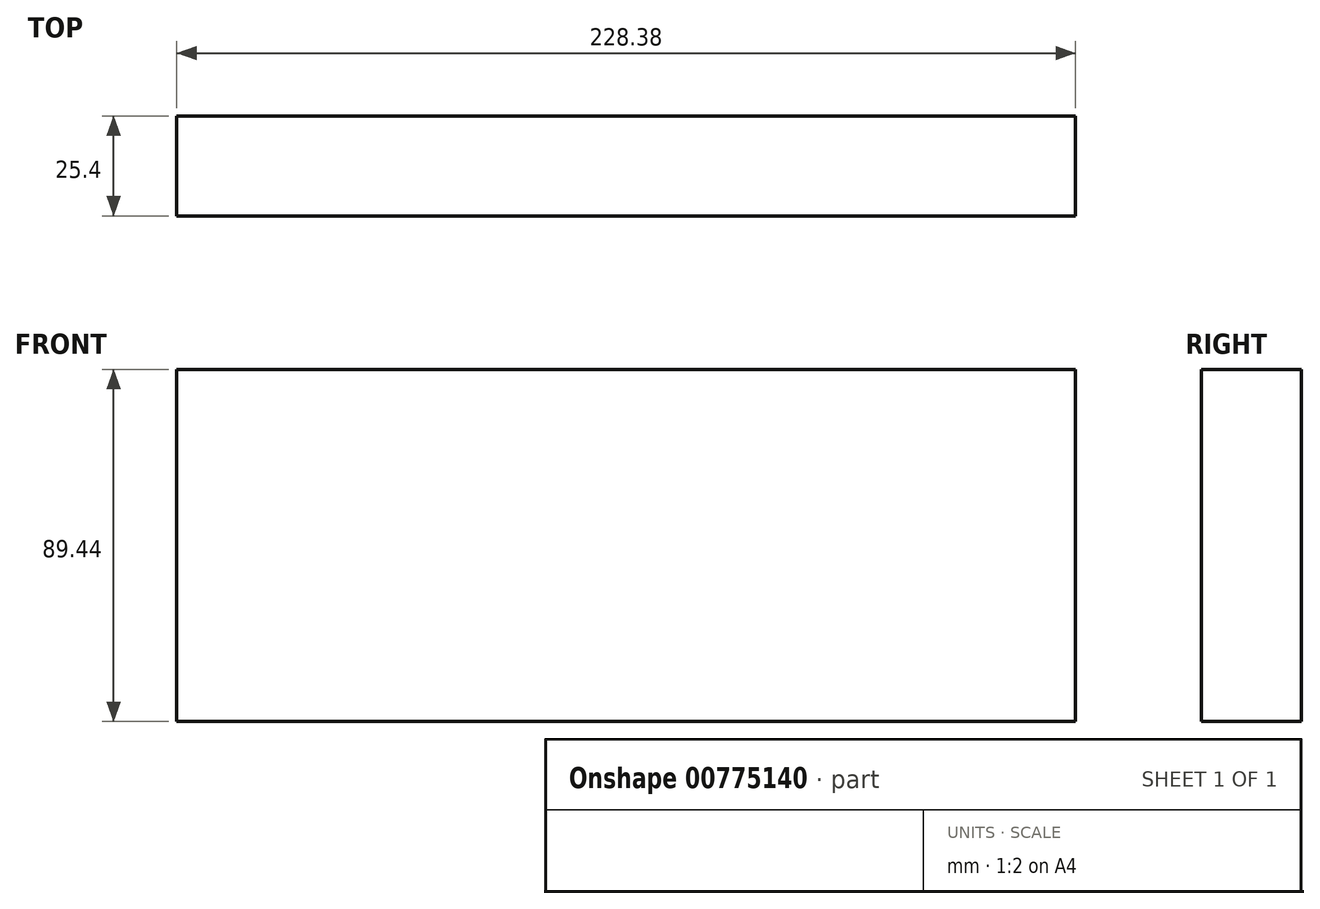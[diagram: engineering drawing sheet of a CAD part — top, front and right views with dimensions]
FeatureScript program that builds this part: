
annotation { "Feature Type Name" : "Feature", "Feature Type Description" : "" }
export const myFeature = defineFeature(function(context is Context, id is Id, definition is map)
    precondition{}
    {
        {
            var Q0;
            Q0=qCreatedBy(makeId("Front.planeOp"),FACE);
            var sketch = newSketch(context, id + "F0", { "sketchPlane" : qUnion([Q0])});
            skLineSegment(sketch, "E0.bottom", {"start": v(114.2, -44.72) * mm, "end": v(-114.2, -44.72) * mm});
            skLineSegment(sketch, "E0.top", {"start": v(114.2, 44.72) * mm, "end": v(-114.2, 44.72) * mm});
            skLineSegment(sketch, "E0.left", {"start": v(114.2, -44.72) * mm, "end": v(114.2, 44.72) * mm});
            skLineSegment(sketch, "E0.right", {"start": v(-114.2, -44.72) * mm, "end": v(-114.2, 44.72) * mm});
            skPoint(sketch, "E0.middle", {"position": v(0, 0) * mm});
            skSolve(sketch);
        }
        {
            var Q0;
            Q0 = qSketchRegion(id + "F0", true);
            extrude(context, id + "F1", {"entities" : qUnion([Q0]), "depth" : 25.4 * mm, "offsetDistance" : 25.4 * mm});
        }
    });
